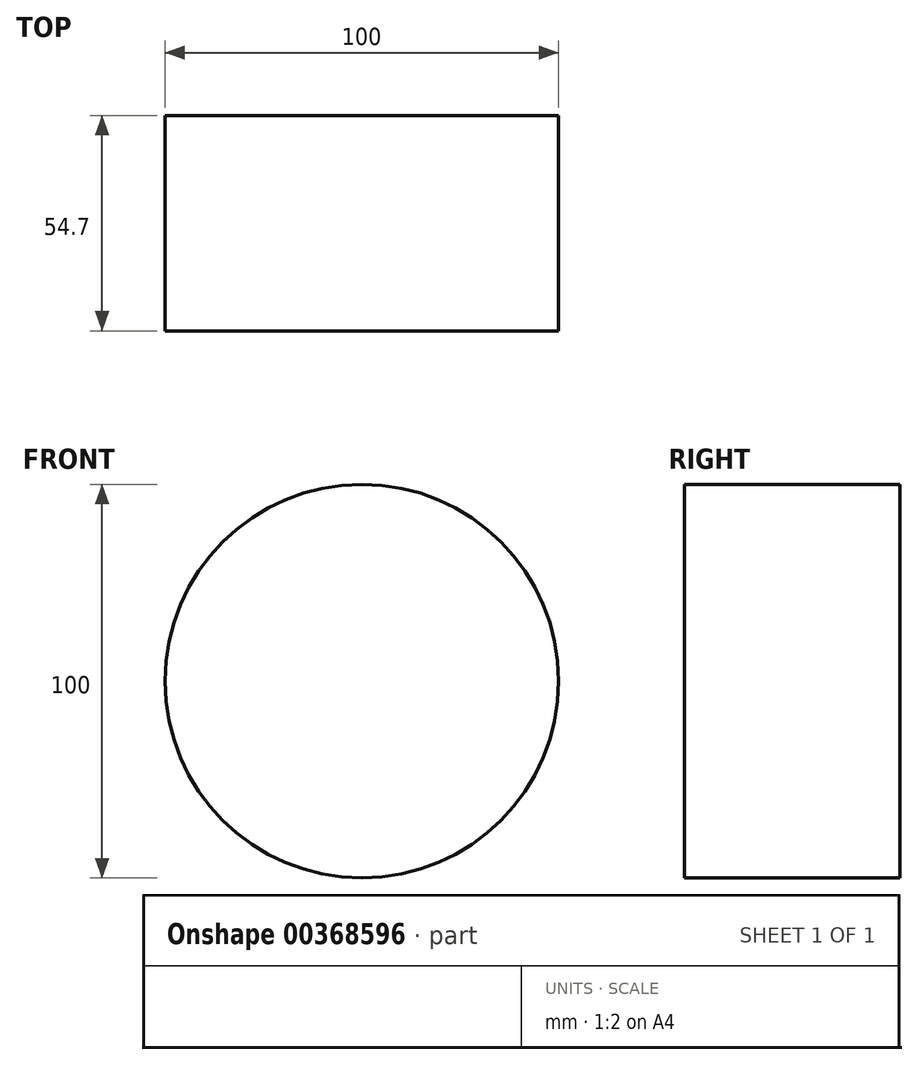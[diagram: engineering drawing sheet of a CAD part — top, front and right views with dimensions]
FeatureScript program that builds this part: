
annotation { "Feature Type Name" : "Feature", "Feature Type Description" : "" }
export const myFeature = defineFeature(function(context is Context, id is Id, definition is map)
    precondition{}
    {
        {
            var Q0;
            Q0=qCreatedBy(makeId("Front.planeOp"),FACE);
            var sketch = newSketch(context, id + "F0", { "sketchPlane" : qUnion([Q0])});
            skCircle(sketch, "E0", {"center": v(0, 0) * mm, "radius": 50 * mm});
            skSolve(sketch);
        }
        {
            var Q0;
            Q0=makeQuery(id+"F0.imprint","IMPRINT",FACE,{"disambiguationData":[TD([[makeQuery(id+"F0.imprint","IMPRINT",EDGE,{"derivedFrom":sQuery(id+"F0.wireOp",EDGE,"E0")}),1.0]])]});
            extrude(context, id + "F1", {"entities" : qUnion([Q0]), "depth" : 54.7 * mm});
        }
    });
